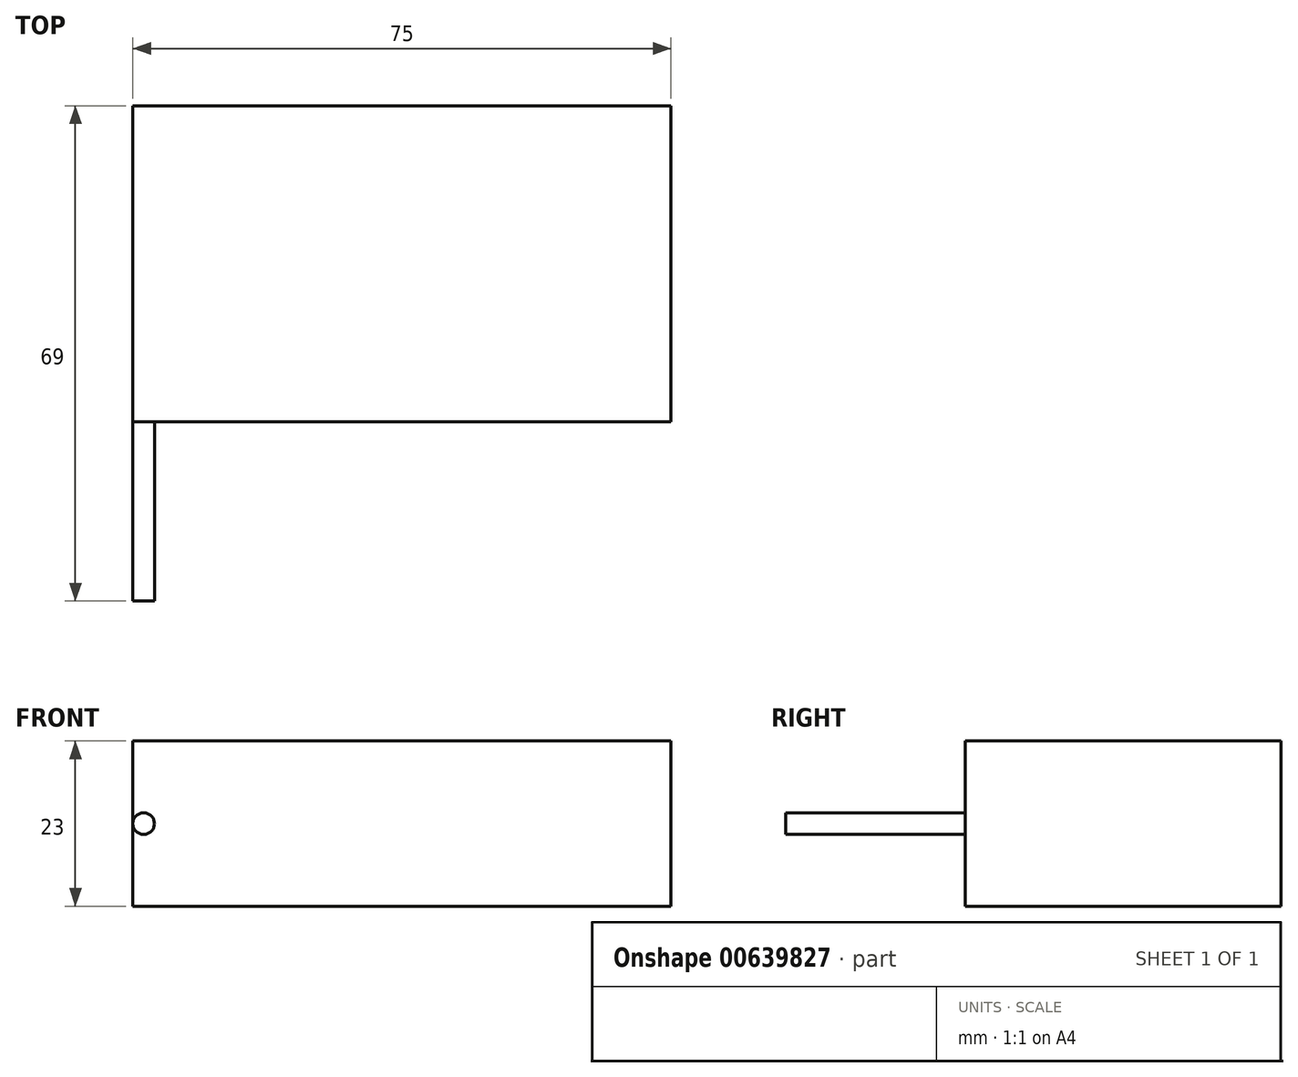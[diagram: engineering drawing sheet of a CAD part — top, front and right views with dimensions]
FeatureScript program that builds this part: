
annotation { "Feature Type Name" : "Feature", "Feature Type Description" : "" }
export const myFeature = defineFeature(function(context is Context, id is Id, definition is map)
    precondition{}
    {
        {
            var Q0;
            Q0=qCreatedBy(makeId("Top.planeOp"),FACE);
            var sketch = newSketch(context, id + "F0", { "sketchPlane" : qUnion([Q0])});
            skLineSegment(sketch, "E0.bottom", {"start": v(-37.5, -22) * mm, "end": v(-15.1, -22) * mm});
            skLineSegment(sketch, "E0.top", {"start": v(-37.5, 22) * mm, "end": v(37.5, 22) * mm});
            skLineSegment(sketch, "E0.left", {"start": v(-37.5, -22) * mm, "end": v(-37.5, 22) * mm});
            skLineSegment(sketch, "E0.right", {"start": v(37.5, -22) * mm, "end": v(37.5, 22) * mm});
            skPoint(sketch, "E0.middle", {"position": v(0, 0) * mm});
            skLineSegment(sketch, "E1", {"start": v(-15.1, -22) * mm, "end": v(37.5, -22) * mm});
            skLineSegment(sketch, "E2", {"start": v(-15.1, -22) * mm, "end": v(-15.1, 22) * mm, "construction": true});
            skCircle(sketch, "E3", {"center": v(-15.1, -23.5) * mm, "radius": 1.5 * mm});
            skLineSegment(sketch, "E4", {"start": v(-15.1, -22) * mm, "end": v(-15.1, -23.5) * mm, "construction": true});
            skCircle(sketch, "E5", {"center": v(-15.1, 23.5) * mm, "radius": 1.5 * mm});
            skLineSegment(sketch, "E6", {"start": v(-15.1, 22) * mm, "end": v(-15.1, 23.5) * mm, "construction": true});
            skSolve(sketch);
        }
        {
            var Q0;
            Q0=makeQuery(id+"F0.imprint","IMPRINT",FACE,{"disambiguationData":[TD([[makeQuery(id+"F0.imprint","IMPRINT",EDGE,{"derivedFrom":sQuery(id+"F0.wireOp",EDGE,"E0.bottom")}),1.0]])]});
            extrude(context, id + "F1", {"entities" : qUnion([Q0]), "depth" : 23 * mm, "offsetDistance" : 25 * mm});
        }
        {
            var Q0;
            Q0=makeQuery(id+"F1.opExtrude","SWEPT_FACE",FACE,{"disambiguationData":[OSD([sQuery(id+"F0.wireOp",EDGE,"E0.bottom"),sQuery(id+"F0.wireOp",EDGE,"E1")])]});
            var sketch = newSketch(context, id + "F2", { "sketchPlane" : qUnion([Q0])});
            skCircle(sketch, "E7", {"center": v(-36, 11.5) * mm, "radius": 1.5 * mm});
            skLineSegment(sketch, "E8", {"start": v(-37.5, 23) * mm, "end": v(-37.5, 11.5) * mm, "construction": true});
            skLineSegment(sketch, "E9", {"start": v(-37.5, 11.5) * mm, "end": v(-37.5, 0) * mm, "construction": true});
            skLineSegment(sketch, "E10", {"start": v(-37.5, 11.5) * mm, "end": v(-36, 11.5) * mm, "construction": true});
            skSolve(sketch);
        }
        {
            var Q0;
            Q0=makeQuery(id+"F2.imprint","IMPRINT",FACE,{"disambiguationData":[TD([[makeQuery(id+"F2.imprint","IMPRINT",EDGE,{"derivedFrom":sQuery(id+"F2.wireOp",EDGE,"E7")}),1.0]])]});
            extrude(context, id + "F3", {"entities" : qUnion([Q0]), "operationType" : NewBodyOperationType.ADD, "depth" : 25 * mm, "offsetDistance" : 25 * mm});
        }
        {
            var Q0;
            Q0=makeQuery(id+"F1.opExtrude","SWEPT_FACE",FACE,{"disambiguationData":[OSD([sQuery(id+"F0.wireOp",EDGE,"E0.top")])]});
            var sketch = newSketch(context, id + "F4", { "sketchPlane" : qUnion([Q0])});
            skLineSegment(sketch, "E11", {"start": v(37.5, 0) * mm, "end": v(37.5, 11.5) * mm, "construction": true});
            skLineSegment(sketch, "E12", {"start": v(37.5, 11.5) * mm, "end": v(37.5, 23) * mm, "construction": true});
            skCircle(sketch, "E13", {"center": v(36, 11.5) * mm, "radius": 1.5 * mm});
            skLineSegment(sketch, "E14", {"start": v(37.5, 11.5) * mm, "end": v(36, 11.5) * mm, "construction": true});
            skSolve(sketch);
        }
        {
            var Q0;
            Q0=sQuery(id+"F4.wireOp",EDGE,"E13");
            extrude(context, id + "F5", {"bodyType" : ToolBodyType.SURFACE, "surfaceEntities" : qUnion([Q0]), "depth" : 25 * mm, "offsetDistance" : 25 * mm});
        }
    });
